# Revit family: SeatingInc-Round_Table
name_source: partatom
category: Furniture
revit_build: Autodesk Revit MEP 2014 (Build: 20130308_1515(x64)
units: mm (PartAtom-declared; Revit-internal decimal feet)

## types (10) — shared parameters
Assembly Code = E2020200
Edge Band = STI - Black
Glide = STI - Black
Keynote = 12500
Leg = STI - Metal
Manufacturer = seating inc.
Table Top = STI - Maple
Type Comments = Table Round
URL = http://www.seatinginc.com

## per-type parameters (varying)
| type | Description | Diameter | Half Dia | Height | Leg Offset | Model |
| Round-Table MS18R | Round Table 18"D 16"H | 18" | 9" | 16" | 3 249/256" | MS18R |
| Round-Table MS24R | Round Table 24"D 16"H | 24" | 12" | 16" | 4 209/256" | MS24R |
| Round-Table MS30R | Round Table 30"D 16"H | 30" | 15" | 16" | 5 175/256" | MS30R |
| Round-Table MS36R | Round Table 36"D 16"H | 36" | 18" | 16" | 6 149/256" | MS36R |
| Round-Table MS42R | Round Table 42"D 16"H | 42" | 21" | 16" | 7 127/256" | MS42R |
| Round-Table Tall MT18R | Round-Table Tall 18"D 21"H | 18" | 9" | 21" | 3 249/256" | MT18R |
| Round-Table Tall MT24R | Round-Table Tall 24"D 21"H | 24" | 12" | 21" | 4 209/256" | MT24R |
| Round-Table Tall MT30R | Round-Table Tall 30"D 21"H | 30" | 15" | 21" | 5 175/256" | MT30R |
| Round-Table Tall MT36R | Round-Table Tall 36"D 21"H | 36" | 18" | 21" | 6 149/256" | MT36R |
| Round-Table Tall MT42R | Round-Table Tall 42"D 21"H | 42" | 21" | 21" | 7 127/256" | MT42R |

## geometry (parser evidence)
native form markers: Sweep x1
no freeform markers — native parametric forms only
